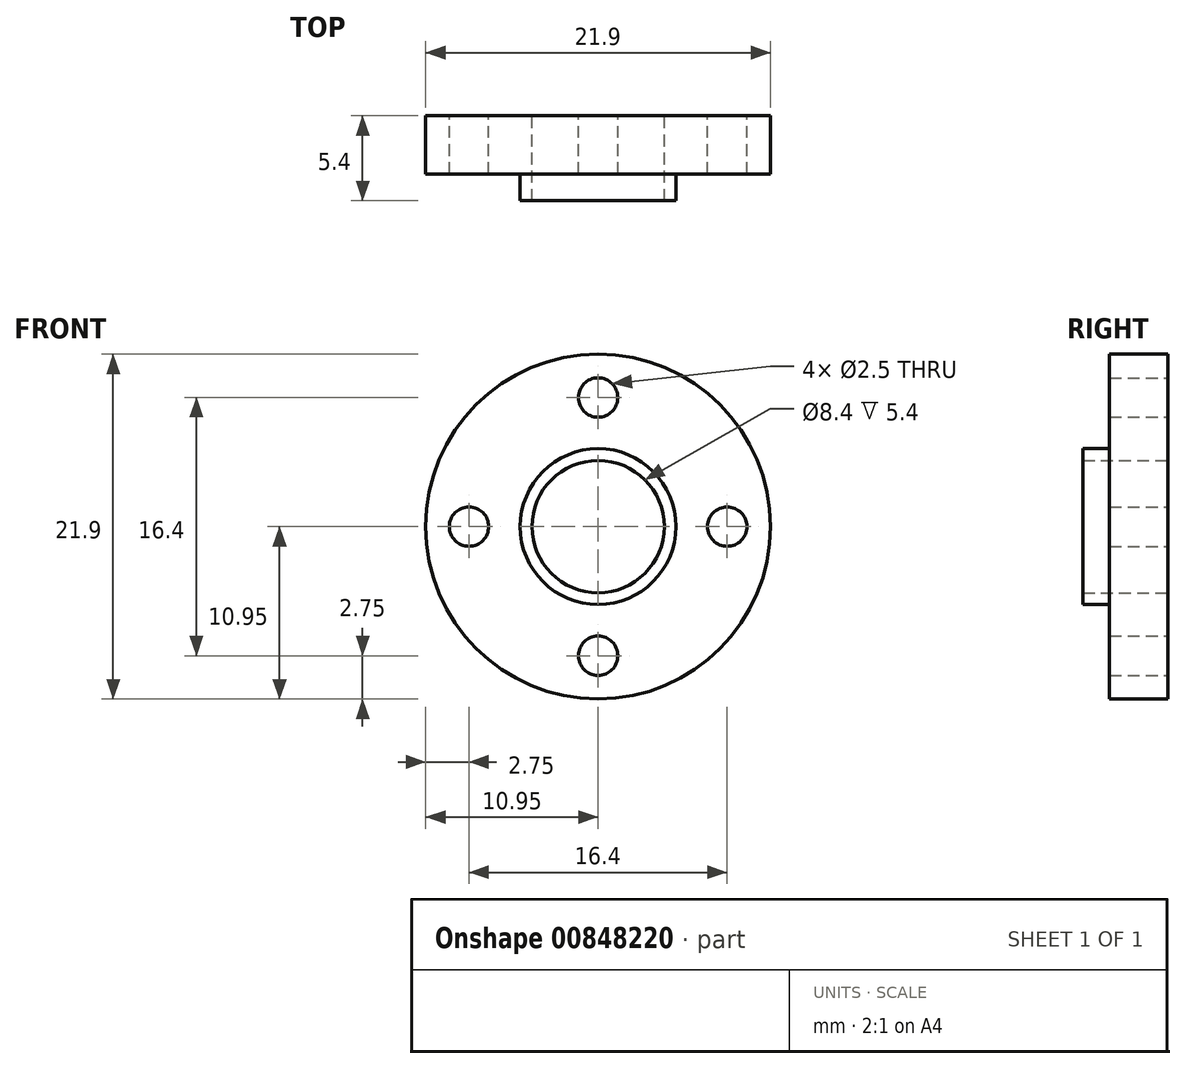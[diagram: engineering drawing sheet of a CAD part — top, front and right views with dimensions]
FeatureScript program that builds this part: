
annotation { "Feature Type Name" : "Feature", "Feature Type Description" : "" }
export const myFeature = defineFeature(function(context is Context, id is Id, definition is map)
    precondition{}
    {
        {
            var Q0;
            Q0=qCreatedBy(makeId("Front.planeOp"),FACE);
            var sketch = newSketch(context, id + "F0", { "sketchPlane" : qUnion([Q0])});
            skCircle(sketch, "E0", {"center": v(0, 0) * mm, "radius": 10.95 * mm});
            skCircle(sketch, "E1", {"center": v(0, 0) * mm, "radius": 4.95 * mm});
            skCircle(sketch, "E2", {"center": v(0, 0) * mm, "radius": 4.2 * mm});
            skCircle(sketch, "E3", {"center": v(0, -8.2) * mm, "radius": 1.25 * mm});
            skCircle(sketch, "E4", {"center": v(8.2, 0) * mm, "radius": 1.25 * mm});
            skCircle(sketch, "E5", {"center": v(0, 8.2) * mm, "radius": 1.25 * mm});
            skCircle(sketch, "E6", {"center": v(-8.2, 0) * mm, "radius": 1.25 * mm});
            skSolve(sketch);
        }
        {
            var Q0;
            Q0=makeQuery(id+"F0.imprint","IMPRINT",FACE,{"disambiguationData":[TD([[makeQuery(id+"F0.imprint","IMPRINT",EDGE,{"derivedFrom":sQuery(id+"F0.wireOp",EDGE,"E1")}),1.0]])]});
            extrude(context, id + "F1", {"entities" : qUnion([Q0]), "depth" : 5.4 * mm, "offsetDistance" : 25 * mm});
        }
        {
            var Q0;
            Q0=makeQuery(id+"F0.imprint","IMPRINT",FACE,{"disambiguationData":[TD([[makeQuery(id+"F0.imprint","IMPRINT",EDGE,{"derivedFrom":sQuery(id+"F0.wireOp",EDGE,"E0")}),1.0]])]});
            extrude(context, id + "F2", {"entities" : qUnion([Q0]), "operationType" : NewBodyOperationType.ADD, "depth" : 3.7 * mm, "offsetDistance" : 25 * mm});
        }
        {
            var Q0;
            Q0=sQuery(id+"F0.wireOp",EDGE,"E2");
            var Q1;
            Q1=sQuery(id+"F0.wireOp",EDGE,"E1");
            extrude(context, id + "F3", {"bodyType" : ToolBodyType.SURFACE, "surfaceEntities" : qUnion([Q0, Q1]), "oppositeDirection" : true, "depth" : 4.8 * mm, "offsetDistance" : 25 * mm});
        }
    });
